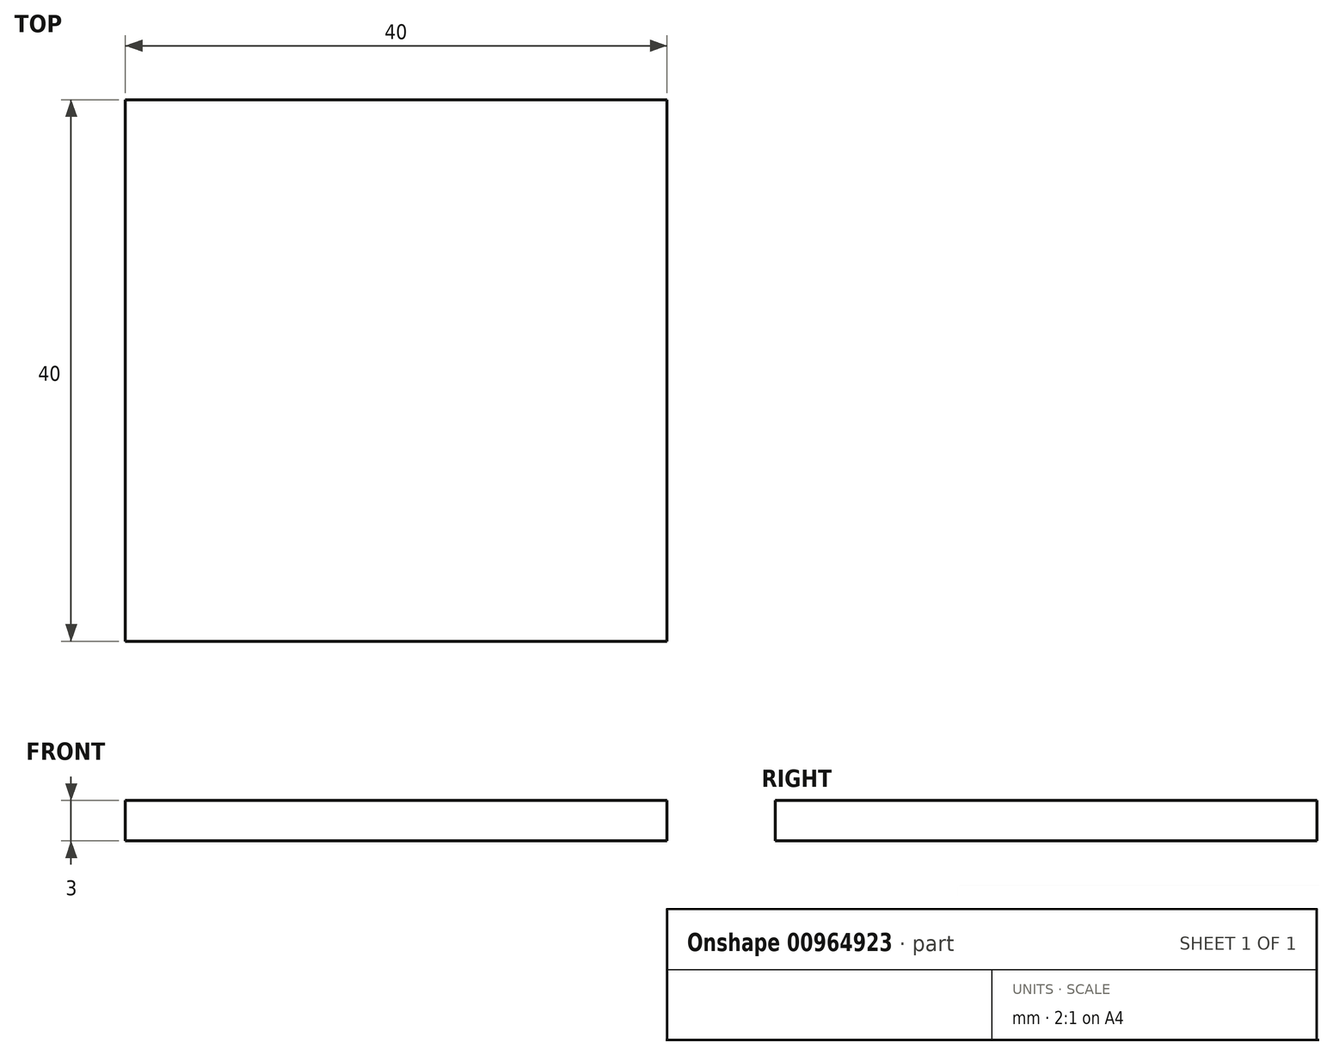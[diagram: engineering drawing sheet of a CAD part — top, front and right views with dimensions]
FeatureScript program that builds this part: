
annotation { "Feature Type Name" : "Feature", "Feature Type Description" : "" }
export const myFeature = defineFeature(function(context is Context, id is Id, definition is map)
    precondition{}
    {
        {
            var Q0;
            Q0=qCreatedBy(makeId("Top.planeOp"),FACE);
            var sketch = newSketch(context, id + "F0", { "sketchPlane" : qUnion([Q0])});
            skLineSegment(sketch, "E0.bottom", {"start": v(-19.42, 19.85) * mm, "end": v(20.58, 19.85) * mm});
            skLineSegment(sketch, "E0.top", {"start": v(-19.42, -20.15) * mm, "end": v(20.58, -20.15) * mm});
            skLineSegment(sketch, "E0.left", {"start": v(-19.42, 19.85) * mm, "end": v(-19.42, -20.15) * mm});
            skLineSegment(sketch, "E0.right", {"start": v(20.58, 19.85) * mm, "end": v(20.58, -20.15) * mm});
            skSolve(sketch);
        }
        {
            var Q0;
            Q0 = qSketchRegion(id + "F0", true);
            extrude(context, id + "F1", {"entities" : qUnion([Q0]), "depth" : 3 * mm, "offsetDistance" : 25 * mm});
        }
    });
